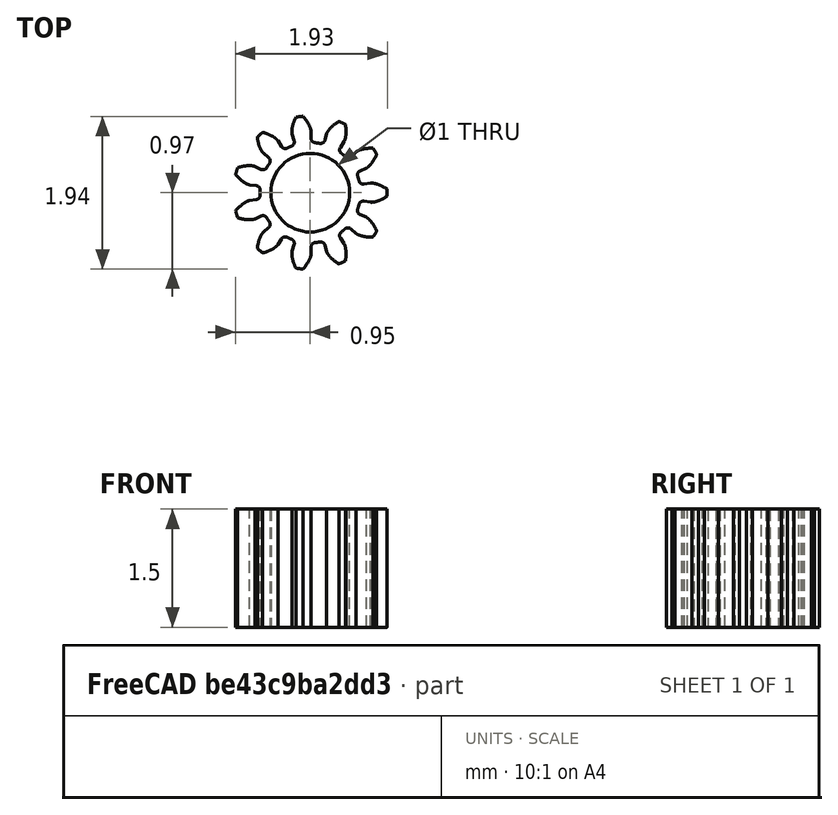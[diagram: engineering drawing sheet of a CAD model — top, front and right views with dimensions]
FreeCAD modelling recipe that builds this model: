
FCSTD DOCUMENT  (FreeCAD 0.18.1R)
Label: Pignion_M015_11
License: All rights reserved
LicenseURL: http://en.wikipedia.org/wiki/All_rights_reserved
objects: Part::Part2DObjectPython×1, PartDesign::Pad×1, Sketcher::SketchObject×1, PartDesign::Pocket×1, PartDesign::Body×1
note: 7 computed .brp shape members not serialized (recipe doc carries the construction recipe); baked Part::Feature solids carry a one-line shape summary decoded from their .brp

FEATURE [Part::Part2DObjectPython] InvoluteGear  # Draft 2D object (typed FeaturePython)
  ExternalGear = true
  HighPrecision = true
  Modules = 0.15
  NumberOfTeeth = 11
  PressureAngle = 20
FEATURE [PartDesign::Pad] Pad
  Length = 1.5
  Length2 = 100
  Profile = -> InvoluteGear
  Type = 0
FEATURE [Sketcher::SketchObject] Sketch
  MapMode = 2
  sketch-geometry (1):
    g0: Circle CenterX=0 CenterY=0 CenterZ=0 NormalX=0 NormalY=0 NormalZ=1 AngleXU=0 Radius=0.5
  constraints (2):
    c: Coincident(g0,g-1)
    c: Radius(g0) = 0.5
FEATURE [PartDesign::Pocket] Pocket
  BaseFeature = -> Pad
  Length = 5
  Length2 = 100
  Profile = -> Sketch
  Reversed = true
  Type = 1
FEATURE [PartDesign::Body] Body
  Group = -> [InvoluteGear,Pad,Sketch,Pocket]
  Origin = -> Origin
  Tip = -> Pocket
